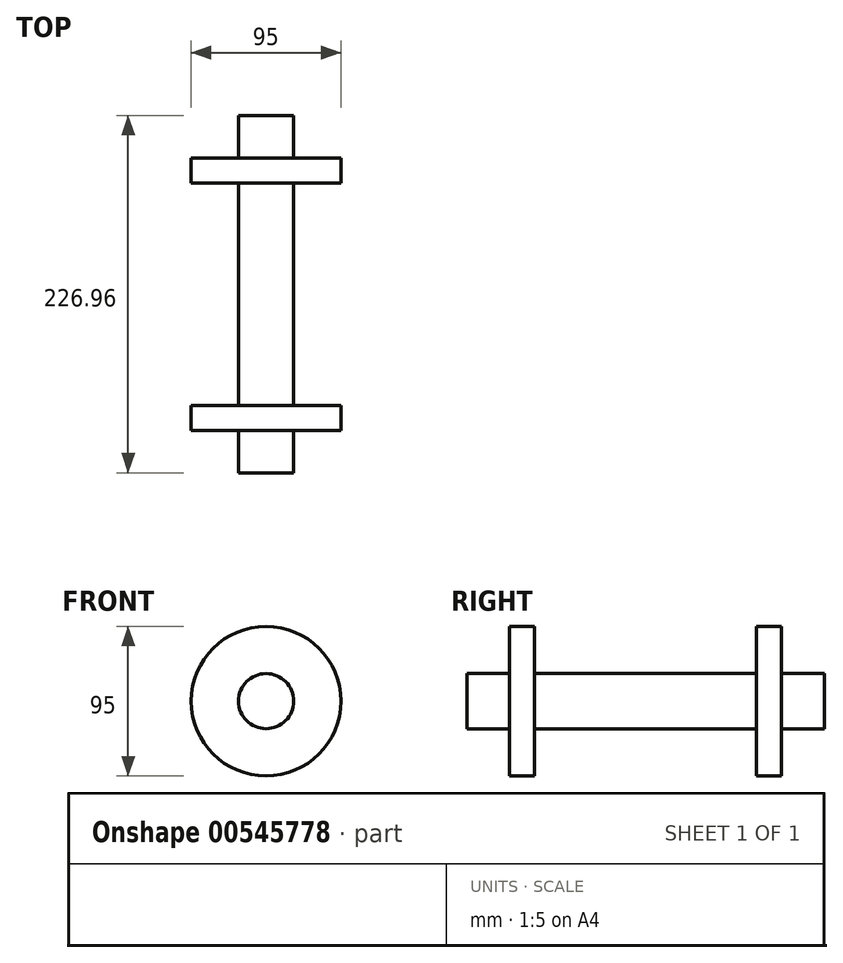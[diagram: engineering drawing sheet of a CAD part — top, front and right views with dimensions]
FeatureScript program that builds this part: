
annotation { "Feature Type Name" : "Feature", "Feature Type Description" : "" }
export const myFeature = defineFeature(function(context is Context, id is Id, definition is map)
    precondition{}
    {
        {
            var Q0;
            Q0=qCreatedBy(makeId("Right.planeOp"),FACE);
            var sketch = newSketch(context, id + "F0", { "sketchPlane" : qUnion([Q0])});
            skLineSegment(sketch, "E0", {"start": v(0, 17.5) * mm, "end": v(70.53, 17.5) * mm});
            skLineSegment(sketch, "E1", {"start": v(70.53, 17.5) * mm, "end": v(70.53, 47.5) * mm});
            skLineSegment(sketch, "E2", {"start": v(70.53, 47.5) * mm, "end": v(86.44, 47.5) * mm});
            skLineSegment(sketch, "E3", {"start": v(86.44, 47.5) * mm, "end": v(86.44, 17.5) * mm});
            skLineSegment(sketch, "E4", {"start": v(86.44, 17.5) * mm, "end": v(113.48, 17.5) * mm});
            skLineSegment(sketch, "E5", {"start": v(113.48, 17.5) * mm, "end": v(113.48, 0) * mm});
            skLineSegment(sketch, "E6", {"start": v(113.48, 0) * mm, "end": v(0, 0) * mm});
            skLineSegment(sketch, "E7", {"start": v(0, 0) * mm, "end": v(0, 17.5) * mm});
            skSolve(sketch);
        }
        {
            var Q0;
            Q0=makeQuery(id+"F0.imprint","IMPRINT",FACE,{"disambiguationData":[TD([[makeQuery(id+"F0.imprint","IMPRINT",EDGE,{"derivedFrom":sQuery(id+"F0.wireOp",EDGE,"E0")}),-1.0]])]});
            var Q1;
            Q1=sQuery(id+"F0.wireOp",EDGE,"E6");
            revolve(context, id + "F1", {"entities" : qUnion([Q0]), "axis" : qUnion([Q1]), "revolveType" : RevolveType.FULL});
        }
        {
            var Q0;
            Q0=makeQuery(id+"F1.opRevolve","SWEPT_BODY",BODY,{"disambiguationData":[OSD([sQuery(id+"F0.wireOp",EDGE,"E0"),sQuery(id+"F0.wireOp",EDGE,"E1"),sQuery(id+"F0.wireOp",EDGE,"E2"),sQuery(id+"F0.wireOp",EDGE,"E3"),sQuery(id+"F0.wireOp",EDGE,"E4"),sQuery(id+"F0.wireOp",EDGE,"E5"),sQuery(id+"F0.wireOp",EDGE,"E6"),sQuery(id+"F0.wireOp",EDGE,"E7")])]});
            var Q1;
            Q1=qCreatedBy(makeId("Front.planeOp"),FACE);
            mirror(context, id + "F2", {"operationType" : NewBodyOperationType.ADD, "entities" : qUnion([Q0]), "mirrorPlane" : qUnion([Q1])});
        }
    });
